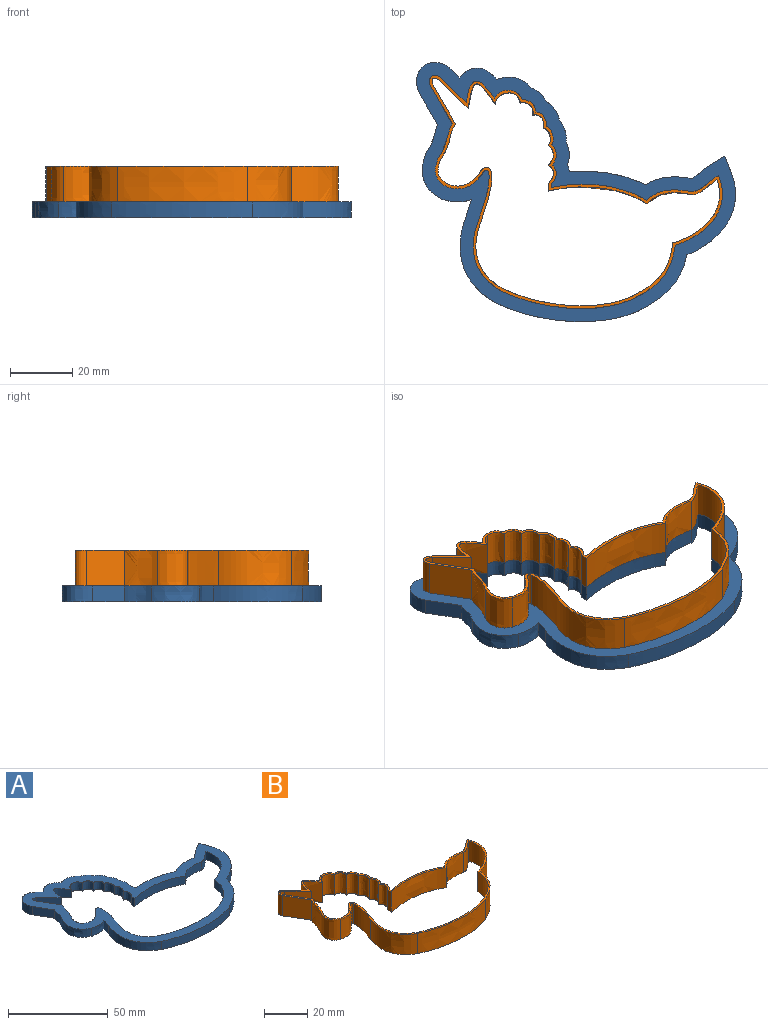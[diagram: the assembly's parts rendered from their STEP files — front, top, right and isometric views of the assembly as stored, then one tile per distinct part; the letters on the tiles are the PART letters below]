
ASSEMBLY  parts=2 mates=1
PART A: 48 faces, bbox 105.9x86.8x8.6 mm
  f0: plane 105.95x86.77mm, normal (0,0,1), area 1677.3mm2, adj f2,f3,f4,f5,f6,f7,f8,f9
  f1: plane 105.95x86.77mm, normal (0,0,-1), area 1677.3mm2, adj f2,f3,f4,f5,f6,f7,f8,f9
  f2: extruded ~11.81x5.08mm, area 72.2mm2, adj f0,f1,f3,f23
  f3: plane 5.08x2.8mm, normal (0.7,0.72,0), area 19.9mm2, adj f0,f1,f2,f4
  f4: extruded ~11.14x9.71mm, area 97.4mm2, adj f0,f1,f3,f5
  f5: plane 10.18x5.95mm, normal (-0.86,-0.5,0), area 59.9mm2, adj f0,f1,f4,f6
  f6: extruded ~8.67x5.08mm, area 47.8mm2, adj f0,f1,f5,f7
  f7: extruded ~15.45x6.66mm, area 94.1mm2, adj f0,f1,f6,f8
  f8: extruded ~9.14x5.08mm, area 47.3mm2, adj f0,f1,f7,f9
  f9: extruded ~5.08x4.67mm, area 24.8mm2, adj f0,f1,f8,f10
  f10: extruded ~28.54x11.45mm, area 169mm2, adj f0,f1,f9,f11
  f11: extruded ~45.18x6.03mm, area 235.9mm2, adj f0,f1,f10,f12
  f12: extruded ~18.27x16.17mm, area 129.2mm2, adj f0,f1,f11,f13
  f13: extruded ~31.67x15.58mm, area 200.1mm2, adj f0,f1,f12,f14
  f14: extruded ~10.5x7.19mm, area 63.9mm2, adj f0,f1,f13,f15
  f15: extruded ~15.06x5.08mm, area 79.1mm2, adj f0,f1,f14,f16
  f16: extruded ~24.42x5.08mm, area 127.5mm2, adj f0,f1,f15,f17
  f17: extruded ~5.08x2.36mm, area 12.3mm2, adj f0,f1,f16,f18
  f18: extruded ~7.1x5.08mm, area 37.3mm2, adj f0,f1,f17,f19
  f19: extruded ~7.1x5.08mm, area 38.8mm2, adj f0,f1,f18,f20
  f20: extruded ~5.82x5.08mm, area 37.4mm2, adj f0,f1,f19,f21
  f21: extruded ~5.12x5.08mm, area 35.7mm2, adj f0,f1,f20,f22
  f22: extruded ~8.57x5.08mm, area 49.2mm2, adj f0,f1,f21,f23
  f23: extruded ~5.08x2.31mm, area 12.3mm2, adj f0,f1,f2,f22
  f24: extruded ~8.65x7.74mm, area 88.9mm2, adj f0,f1,f25,f47
  f25: plane 8.84x8.63mm, normal (-0.7,-0.72,0), area 62.7mm2, adj f0,f1,f24,f26
  f26: extruded ~5.08x2.64mm, area 25.5mm2, adj f0,f1,f25,f27
  f27: plane 12.33x7.21mm, normal (0.86,0.5,0), area 72.5mm2, adj f0,f1,f26,f28
  f28: extruded ~11.23x5.08mm, area 62.5mm2, adj f0,f1,f27,f29
  f29: extruded ~8.19x5.08mm, area 49.7mm2, adj f0,f1,f28,f30
  f30: extruded ~10.06x5.08mm, area 59.4mm2, adj f0,f1,f29,f31
  f31: extruded ~5.08x3.77mm, area 26.9mm2, adj f0,f1,f30,f32
  f32: extruded ~14.97x5.08mm, area 78.2mm2, adj f0,f1,f31,f33
  f33: extruded ~22.38x8.7mm, area 132.4mm2, adj f0,f1,f32,f34
  f34: extruded ~40.73x5.46mm, area 212.6mm2, adj f0,f1,f33,f35
  f35: extruded ~17.43x13.78mm, area 119.2mm2, adj f0,f1,f34,f36
  f36: extruded ~20.35x15.01mm, area 142.4mm2, adj f0,f1,f35,f37
  f37: extruded ~7.88x5.08mm, area 47.7mm2, adj f0,f1,f36,f38
  f38: extruded ~14.6x5.08mm, area 79.5mm2, adj f0,f1,f37,f39
  f39: extruded ~31.63x5.47mm, area 166.3mm2, adj f0,f1,f38,f40
  f40: plane 5.08x2.52mm, normal (-1,0,0), area 12.8mm2, adj f0,f1,f39,f41
  f41: extruded ~5.58x5.08mm, area 34.6mm2, adj f0,f1,f40,f42
  f42: extruded ~6.46x5.08mm, area 38mm2, adj f0,f1,f41,f43
  f43: extruded ~5.47x5.08mm, area 33.8mm2, adj f0,f1,f42,f44
  f44: extruded ~5.08x4.39mm, area 34.5mm2, adj f0,f1,f43,f45
  f45: extruded ~5.08x4.09mm, area 34.7mm2, adj f0,f1,f44,f46
  f46: extruded ~5.08x4.45mm, area 31.3mm2, adj f0,f1,f45,f47
  f47: extruded ~5.08x3.68mm, area 27.6mm2, adj f0,f1,f24,f46
PART B: 50 faces, bbox 97.1x77.7x14.3 mm
  f0: plane 97.05x77.74mm, normal (0,0,1), area 292.6mm2, adj f2,f3,f4,f5,f6,f7,f8,f9
  f1: plane 97.05x77.74mm, normal (0,0,-1), area 292.6mm2, adj f2,f3,f4,f5,f6,f7,f8,f9
  f2: extruded ~11.43x9.02mm, area 185.1mm2, adj f0,f1,f3,f25
  f3: plane 11.43x7.64mm, normal (0.7,0.72,0), area 122mm2, adj f0,f1,f2,f4
  f4: extruded ~11.43x4.13mm, area 85.5mm2, adj f0,f1,f3,f5
  f5: plane 11.89x11.43mm, normal (-0.86,-0.5,0), area 157.4mm2, adj f0,f1,f4,f6
  f6: extruded ~11.43x10.84mm, area 135.1mm2, adj f0,f1,f5,f7
  f7: extruded ~11.43x9.46mm, area 129.2mm2, adj f0,f1,f6,f8
  f8: extruded ~11.43x11.15mm, area 147.9mm2, adj f0,f1,f7,f9
  f9: extruded ~11.43x2.11mm, area 35.9mm2, adj f0,f1,f8,f10
  f10: extruded ~14.52x11.43mm, area 170.9mm2, adj f0,f1,f9,f11
  f11: extruded ~23.46x11.43mm, area 312.3mm2, adj f0,f1,f10,f12
  f12: extruded ~41.51x11.43mm, area 487.6mm2, adj f0,f1,f11,f13
  f13: extruded ~17.56x14.21mm, area 272.1mm2, adj f0,f1,f12,f14
  f14: extruded ~22.35x15.09mm, area 342.8mm2, adj f0,f1,f13,f15
  f15: extruded ~11.43x8.27mm, area 113.1mm2, adj f0,f1,f14,f16
  f16: extruded ~14.78x11.43mm, area 179.3mm2, adj f0,f1,f15,f17
  f17: extruded ~30.62x11.43mm, area 361.5mm2, adj f0,f1,f16,f18
  f18: plane 11.43x0.99mm, normal (1,0,0), area 11.3mm2, adj f0,f1,f17,f19
  f19: extruded ~11.43x6.2mm, area 80.5mm2, adj f0,f1,f18,f20
  f20: extruded ~11.43x6.46mm, area 81.3mm2, adj f0,f1,f19,f21
  f21: extruded ~11.43x5.91mm, area 76.9mm2, adj f0,f1,f20,f22
  f22: extruded ~11.43x4.63mm, area 74.1mm2, adj f0,f1,f21,f23
  f23: extruded ~11.43x4.33mm, area 74.7mm2, adj f0,f1,f22,f24
  f24: extruded ~11.43x5.23mm, area 75.7mm2, adj f0,f1,f23,f25
  f25: extruded ~11.43x3.77mm, area 53.2mm2, adj f0,f1,f2,f24
  f26: extruded ~11.43x8.65mm, area 200.1mm2, adj f0,f1,f27,f49
  f27: plane 11.43x8.84mm, normal (-0.7,-0.72,0), area 141.2mm2, adj f0,f1,f26,f28
  f28: extruded ~11.43x2.64mm, area 57.4mm2, adj f0,f1,f27,f29
  f29: plane 12.33x11.43mm, normal (0.86,0.5,0), area 163.2mm2, adj f0,f1,f28,f30
  f30: extruded ~11.43x11.23mm, area 140.6mm2, adj f0,f1,f29,f31
  f31: extruded ~11.43x8.19mm, area 111.8mm2, adj f0,f1,f30,f32
  f32: extruded ~11.43x10.06mm, area 133.6mm2, adj f0,f1,f31,f33
  f33: extruded ~11.43x3.77mm, area 60.6mm2, adj f0,f1,f32,f34
  f34: extruded ~14.97x11.43mm, area 176mm2, adj f0,f1,f33,f35
  f35: extruded ~22.38x11.43mm, area 297.8mm2, adj f0,f1,f34,f36
  f36: extruded ~40.73x11.43mm, area 478.4mm2, adj f0,f1,f35,f37
  f37: extruded ~17.43x13.78mm, area 268.3mm2, adj f0,f1,f36,f38
  f38: extruded ~20.35x15.01mm, area 320.3mm2, adj f0,f1,f37,f39
  f39: extruded ~11.43x7.88mm, area 107.3mm2, adj f0,f1,f38,f40
  f40: extruded ~14.6x11.43mm, area 178.9mm2, adj f0,f1,f39,f41
  f41: extruded ~31.63x11.43mm, area 374.3mm2, adj f0,f1,f40,f42
  f42: plane 11.43x2.52mm, normal (-1,0,0), area 28.8mm2, adj f0,f1,f41,f43
  f43: extruded ~11.43x5.58mm, area 77.8mm2, adj f0,f1,f42,f44
  f44: extruded ~11.43x6.46mm, area 85.6mm2, adj f0,f1,f43,f45
  f45: extruded ~11.43x5.47mm, area 76.1mm2, adj f0,f1,f44,f46
  f46: extruded ~11.43x4.39mm, area 77.5mm2, adj f0,f1,f45,f47
  f47: extruded ~11.43x4.09mm, area 78mm2, adj f0,f1,f46,f48
  f48: extruded ~11.43x4.45mm, area 70.3mm2, adj f0,f1,f47,f49
  f49: extruded ~11.43x3.68mm, area 62.1mm2, adj f0,f1,f26,f48
PLACE A at identity
PLACE B t=(101.31,-9.79,5.08)mm
MATE fastened B.f1 <-> A.f0  axis (0,0,-1) through (123.75,-8.21,5.08)mm
